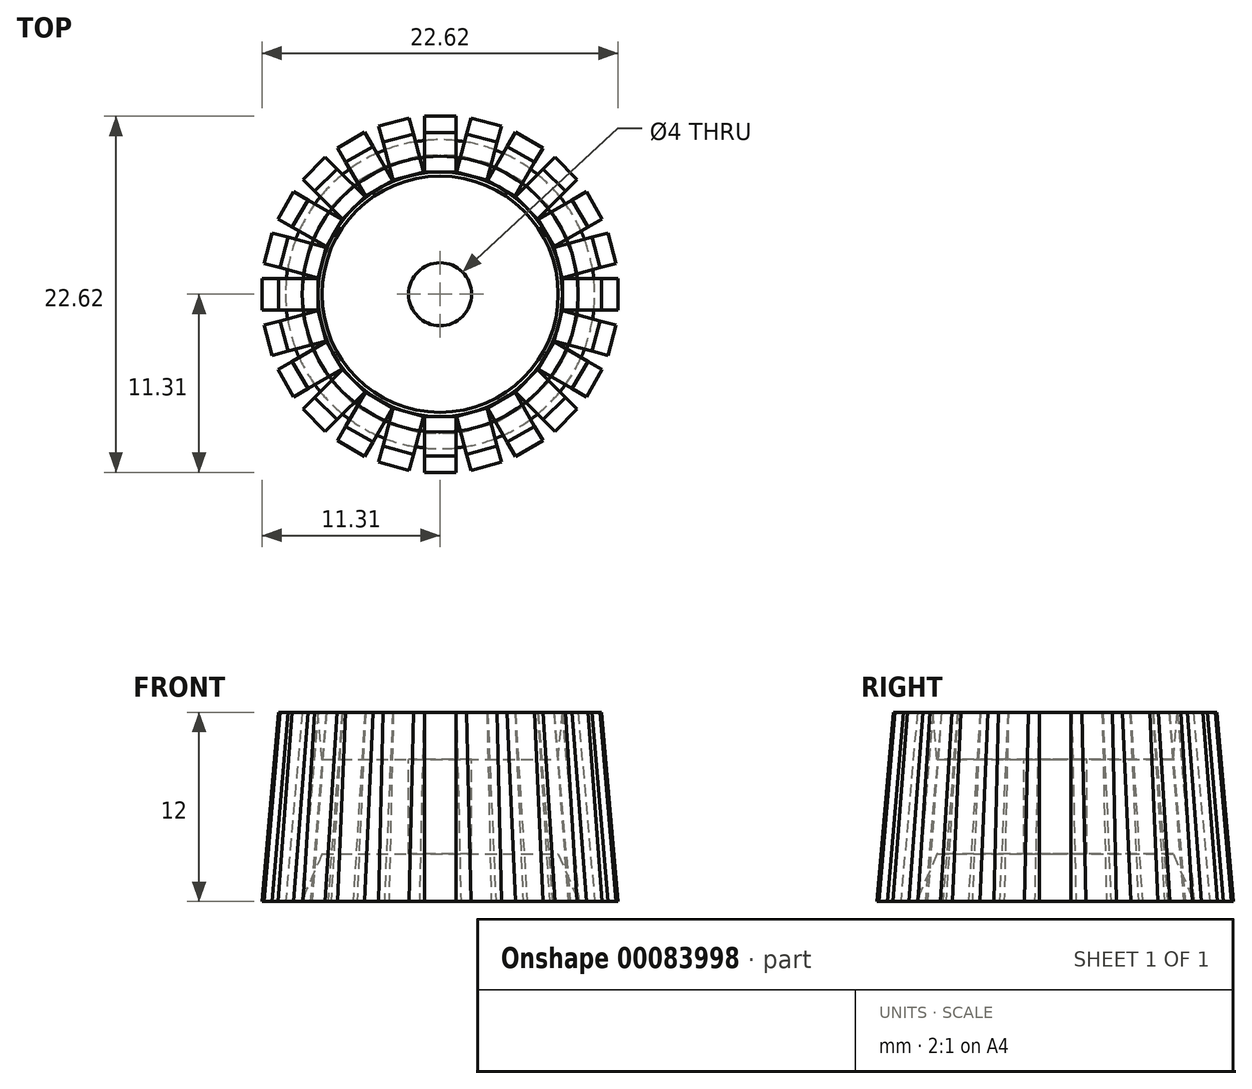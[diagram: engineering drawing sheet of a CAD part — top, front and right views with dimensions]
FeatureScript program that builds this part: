
annotation { "Feature Type Name" : "Feature", "Feature Type Description" : "" }
export const myFeature = defineFeature(function(context is Context, id is Id, definition is map)
    precondition{}
    {
        {
            var Q0;
            Q0=qCreatedBy(makeId("Front.planeOp"),FACE);
            var sketch = newSketch(context, id + "F0", { "sketchPlane" : qUnion([Q0])});
            skLineSegment(sketch, "E0", {"start": v(0, 0) * mm, "end": v(7.5, 0) * mm});
            skLineSegment(sketch, "E1", {"start": v(7.5, 0) * mm, "end": v(7.76, 3) * mm});
            skLineSegment(sketch, "E2", {"start": v(7.76, 3) * mm, "end": v(8.76, 3) * mm});
            skLineSegment(sketch, "E3", {"start": v(8.76, 3) * mm, "end": v(9.81, -9) * mm});
            skLineSegment(sketch, "E4", {"start": v(9.81, -9) * mm, "end": v(8.81, -9) * mm});
            skLineSegment(sketch, "E5", {"start": v(8.81, -9) * mm, "end": v(7.5, -6) * mm});
            skLineSegment(sketch, "E6", {"start": v(7.5, -6) * mm, "end": v(0, -6) * mm});
            skLineSegment(sketch, "E7", {"start": v(0, -6) * mm, "end": v(0, 0) * mm});
            skSolve(sketch);
        }
        {
            var Q0;
            Q0=makeQuery(id+"F0.imprint","IMPRINT",FACE,{"disambiguationData":[TD([[makeQuery(id+"F0.imprint","IMPRINT",EDGE,{"derivedFrom":sQuery(id+"F0.wireOp",EDGE,"E0")}),-1.0]])]});
            var Q1;
            Q1=sQuery(id+"F0.wireOp",EDGE,"E7");
            revolve(context, id + "F1", {"entities" : qUnion([Q0]), "axis" : qUnion([Q1]), "revolveType" : RevolveType.FULL});
        }
        {
            var Q0;
            Q0=qCreatedBy(makeId("Front.planeOp"),FACE);
            var sketch = newSketch(context, id + "F2", { "sketchPlane" : qUnion([Q0])});
            skLineSegment(sketch, "E8", {"start": v(8.76, 3) * mm, "end": v(10.26, 3) * mm});
            skLineSegment(sketch, "E9", {"start": v(10.26, 3) * mm, "end": v(11.31, -9) * mm});
            skLineSegment(sketch, "E10", {"start": v(11.31, -9) * mm, "end": v(9.81, -9) * mm});
            skLineSegment(sketch, "E11.0", {"start": v(8.76, 3) * mm, "end": v(-8.76, 3) * mm, "construction": true});
            skLineSegment(sketch, "E12.0", {"start": v(9.81, -9) * mm, "end": v(-9.81, -9) * mm, "construction": true});
            skLineSegment(sketch, "E13.0", {"start": v(7.76, 3) * mm, "end": v(-7.76, 3) * mm, "construction": true});
            skLineSegment(sketch, "E14", {"start": v(8.76, 3) * mm, "end": v(9.81, -9) * mm, "construction": true});
            skLineSegment(sketch, "E15", {"start": v(8.76, 3) * mm, "end": v(7.76, 3) * mm});
            skLineSegment(sketch, "E16", {"start": v(7.76, 3) * mm, "end": v(8.81, -9) * mm});
            skLineSegment(sketch, "E17", {"start": v(8.81, -9) * mm, "end": v(9.81, -9) * mm});
            skSolve(sketch);
        }
        {
            var Q0;
            Q0=makeQuery(id+"F2.imprint","IMPRINT",FACE,{"disambiguationData":[TD([[makeQuery(id+"F2.imprint","IMPRINT",EDGE,{"derivedFrom":sQuery(id+"F2.wireOp",EDGE,"E8")}),-1.0]])]});
            extrude(context, id + "F3", {"entities" : qUnion([Q0]), "depth" : 1 * mm, "hasSecondDirection" : true, "secondDirectionOppositeDirection" : true, "secondDirectionDepth" : 1 * mm});
        }
        {
            var Q0;
            Q0=makeQuery(id+"F3.opExtrude","SWEPT_BODY",BODY,{"disambiguationData":[OSD([sQuery(id+"F2.wireOp",EDGE,"E8"),sQuery(id+"F2.wireOp",EDGE,"E9"),sQuery(id+"F2.wireOp",EDGE,"E10"),sQuery(id+"F2.wireOp",EDGE,"E15"),sQuery(id+"F2.wireOp",EDGE,"E16"),sQuery(id+"F2.wireOp",EDGE,"E17")])]});
            var Q1;
            Q1=makeQuery(id+"F1.opRevolve","SWEPT_EDGE",EDGE,{"disambiguationData":[OSD([sQuery(id+"F0.wireOp",EDGE,"E1"),sQuery(id+"F0.wireOp",EDGE,"E2")])]});
            circularPattern(context, id + "F4", {"entities" : qUnion([Q0]), "axis" : qUnion([Q1]), "angle" : 15 * degree, "instanceCount" : 24});
        }
        {
            var Q0;
            Q0=makeQuery(id+"F1.opRevolve","SWEPT_FACE",FACE,{"disambiguationData":[OSD([sQuery(id+"F0.wireOp",EDGE,"E0")])]});
            var sketch = newSketch(context, id + "F5", { "sketchPlane" : qUnion([Q0])});
            skCircle(sketch, "E18", {"center": v(0, 0) * mm, "radius": 2 * mm});
            skSolve(sketch);
        }
        {
            var Q0;
            Q0 = qSketchRegion(id + "F5", true);
            extrude(context, id + "F6", {"entities" : qUnion([Q0]), "operationType" : NewBodyOperationType.REMOVE, "oppositeDirection" : true, "depth" : 25 * mm});
        }
    });
